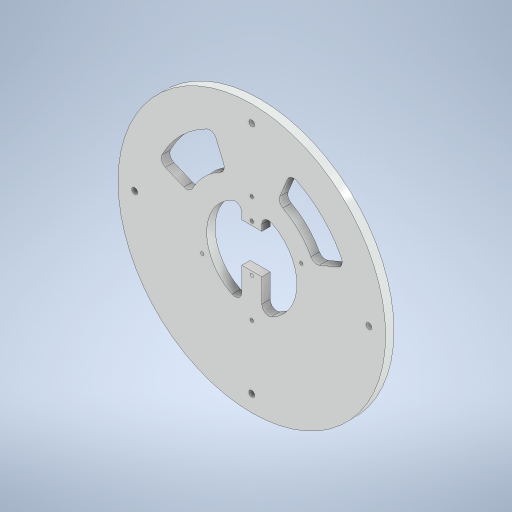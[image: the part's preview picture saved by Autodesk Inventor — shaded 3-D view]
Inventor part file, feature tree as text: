
AUTODESK INVENTOR PART (.ipt)
format: ipt  version: 2023.1 (Build 271208000, 208)  size: 333,824 bytes
history: native  units: mm
features: extrude x5, sketch x4, fillet x2, other x1, pattern_circular x1, mirror x1
ambient origin geometry x8: Origin, YZ Plane, XZ Plane, XY Plane, X Axis, Y Axis, Z Axis, Center Point
bodies: Body1 (feature_tree)
feature tree (14):
  other  "솔리드1"
  sketch  "스케치1"
  extrude  "돌출1"  Depth=160.0mm
  extrude  "돌출2"  Depth=68.0mm
  fillet  "모깎기1"  Radius=54.0mm
  extrude  "돌출3"  Depth=120.0mm
  pattern_circular  "원형 패턴2"  Count=8  [1 undecoded]
  extrude  "돌출4"  TaperAngle=45.0deg  [1 undecoded]
  fillet  "모깎기2"  Radius=5.0mm
  extrude  "돌출5"  Depth=5.0mm TaperAngle=0.0deg
  mirror  "미러1"
  sketch  "스케치2"
  sketch  "스케치3"
  sketch  "스케치4"
note: 2 required parameter values undecoded (feature->parameter linkage not recoverable at this tier; creation-order binding heuristic only, values carry confidence <= 0.55)
